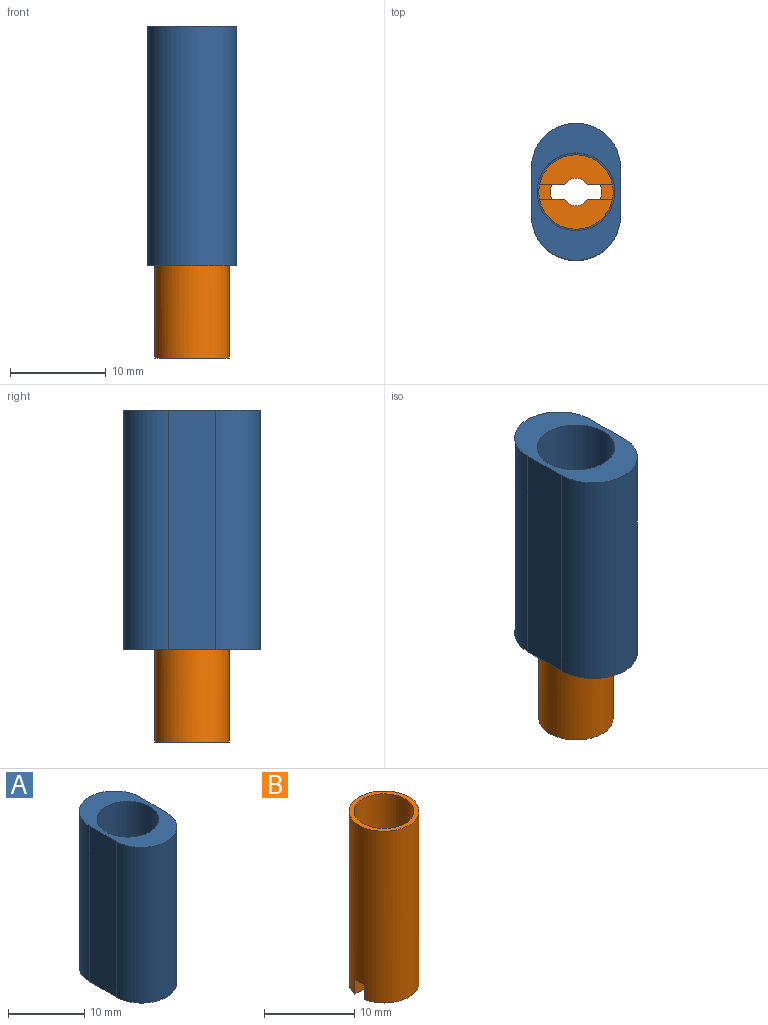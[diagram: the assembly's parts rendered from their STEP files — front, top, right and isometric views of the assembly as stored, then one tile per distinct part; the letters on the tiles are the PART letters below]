
ASSEMBLY  parts=2 mates=1
PART A: 9 faces, bbox 9.3x14.3x25 mm
  f0: cylinder r=3.5mm len=7mm, axis (0,0,-1), area 44mm2, adj f6,f8
  f1: plane 25x5mm, normal (-1,0,0), area 125mm2, adj f2,f4,f5,f6
  f2: cylinder r=4.65mm len=25mm, axis (0,0,-1), area 365.2mm2, adj f1,f3,f5,f6
  f3: plane 25x5mm, normal (1,0,0), area 125mm2, adj f2,f4,f5,f6
  f4: cylinder r=4.65mm len=25mm, axis (0,0,-1), area 365.2mm2, adj f1,f3,f5,f6
  f5: plane 14.3x9.3mm, normal (0,0,1), area 62.6mm2, adj f1,f2,f3,f4,f7
  f6: plane 14.3x9.3mm, normal (0,0,-1), area 75.9mm2, adj f0,f1,f2,f3,f4
  f7: cylinder r=4.06mm len=23mm, axis (0,0,1), area 586.7mm2, adj f5,f8
  f8: plane 8.12x8.12mm, normal (0,0,1), area 13.3mm2, adj f0,f7
PART B: 17 faces, bbox 7.8x7.8x23.3 mm
  f0: plane 7.6x3.13mm, normal (0,0,-1), area 16.6mm2, adj f3,f5,f12,f15
  f1: plane 7.6x3.13mm, normal (0,0,-1), area 16.6mm2, adj f2,f5,f11,f16
  f2: plane 2.57x2mm, normal (0,1,0), area 5.1mm2, adj f1,f4,f5,f13,f16
  f3: plane 2.57x2mm, normal (0,-1,0), area 5.1mm2, adj f0,f5,f10,f13,f15
  f4: plane 5.13x1.92mm, normal (0,0,1), area 6mm2, adj f2,f6,f11,f16
  f5: cylinder r=3.88mm len=23.3mm, axis (0,0,-1), area 561.3mm2, adj f0,f1,f2,f3,f7,f11,f12,f13
  f6: cylinder r=2.67mm len=8.3mm, axis (0,0,-1), area 139.2mm2, adj f4,f9,f10,f13,f14
  f7: plane 7.75x7.75mm, normal (0,0,1), area 12.4mm2, adj f5,f8
  f8: cylinder r=3.32mm len=13mm, axis (0,0,1), area 271.6mm2, adj f7,f9
  f9: plane 6.65x6.65mm, normal (0,0,1), area 12.3mm2, adj f6,f8
  f10: plane 5.13x1.92mm, normal (0,0,1), area 6mm2, adj f3,f6,f12,f15
  f11: plane 2.57x2mm, normal (0,1,0), area 5.1mm2, adj f1,f4,f5,f14,f16
  f12: plane 2.57x2mm, normal (0,-1,0), area 5.1mm2, adj f0,f5,f10,f14,f15
  f13: plane 1.5x1.31mm, normal (0,0,-1), area 1.8mm2, adj f2,f3,f5,f6
  f14: plane 1.5x1.31mm, normal (0,0,-1), area 1.8mm2, adj f5,f6,f11,f12
  f15: cylinder r=1.44mm len=2.47mm, axis (0,0,-1), area 5.9mm2, adj f0,f3,f10,f12
  f16: cylinder r=1.44mm len=2.47mm, axis (0,0,-1), area 5.9mm2, adj f1,f2,f4,f11
PLACE A t=(-25.59,18.17,-11.76)mm fixed
PLACE B rot(axis=(0,1,0),180deg) t=(-3.52,-2.57,1.89)mm
MATE cylindrical B.f5 <-> A.f0  axis (0,0,1) through (-3.52,-2.57,-9.76)mm
